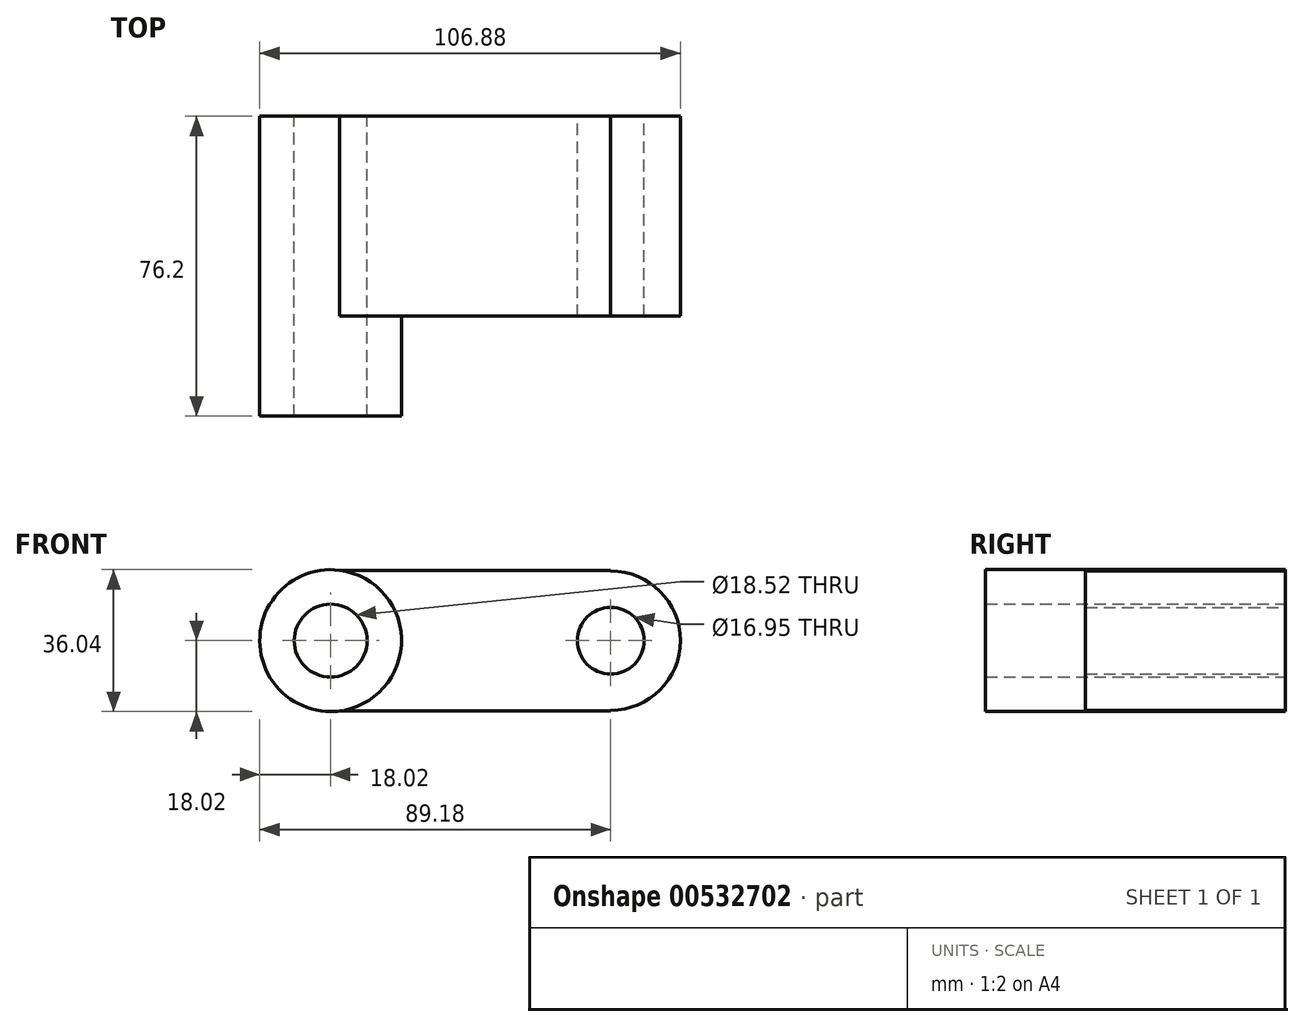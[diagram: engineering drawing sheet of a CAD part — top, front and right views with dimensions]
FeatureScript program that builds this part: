
annotation { "Feature Type Name" : "Feature", "Feature Type Description" : "" }
export const myFeature = defineFeature(function(context is Context, id is Id, definition is map)
    precondition{}
    {
        {
            var Q0;
            Q0=qCreatedBy(makeId("Front.planeOp"),FACE);
            var sketch = newSketch(context, id + "F0", { "sketchPlane" : qUnion([Q0])});
            skLineSegment(sketch, "E0.bottom", {"start": v(35.58, 0) * mm, "end": v(-35.58, 0) * mm});
            skLineSegment(sketch, "E0.top", {"start": v(35.58, 17.88) * mm, "end": v(-35.58, 17.88) * mm});
            skLineSegment(sketch, "E1", {"start": v(-35.58, 0) * mm, "end": v(35.58, 0) * mm, "construction": true});
            skLineSegment(sketch, "E2.MirrorCS", {"start": v(35.58, -17.88) * mm, "end": v(-35.58, -17.88) * mm});
            skLineSegment(sketch, "E3.MirrorCS", {"start": v(35.58, -17.7) * mm, "end": v(35.58, -17.88) * mm});
            skCircle(sketch, "E4", {"center": v(-35.58, 0) * mm, "radius": 18.02 * mm});
            skArc(sketch, "E5", {"start": v(35.58, -17.7) * mm, "mid": v(53.28, 0) * mm, "end": v(35.58, 17.7) * mm});
            skPoint(sketch, "E6.MirrorCS.end.orphan", {"position": v(-35.58, -17.88) * mm});
            skCircle(sketch, "E7", {"center": v(35.58, 0) * mm, "radius": 8.47 * mm});
            skCircle(sketch, "E8", {"center": v(-35.58, 0) * mm, "radius": 9.26 * mm});
            skLineSegment(sketch, "E9.trimOffspring", {"start": v(35.58, 17.7) * mm, "end": v(35.58, 17.88) * mm});
            skSolve(sketch);
        }
        {
            var Q0;
            Q0=makeQuery(id+"F0.imprint","IMPRINT",FACE,{"disambiguationData":[TD([[makeQuery(id+"F0.imprint","IMPRINT",EDGE,{"derivedFrom":sQuery(id+"F0.wireOp",EDGE,"E8")}),-1.0]])]});
            extrude(context, id + "F1", {"entities" : qUnion([Q0]), "depth" : 76.2 * mm, "offsetDistance" : 25.4 * mm});
        }
        {
            var Q0;
            {var subQ4=sQuery(id+"F0.wireOp",EDGE,"E3.MirrorCS");Q0=makeQuery(id+"F0.imprint","IMPRINT",FACE,{"disambiguationData":[TD([[makeQuery(id+"F0.imprint","IMPRINT",EDGE,{"derivedFrom":subQ4}),-1.0]])]});}
            extrude(context, id + "F2", {"entities" : qUnion([Q0]), "operationType" : NewBodyOperationType.ADD, "depth" : 50.8 * mm, "offsetDistance" : 25.4 * mm});
        }
    });
